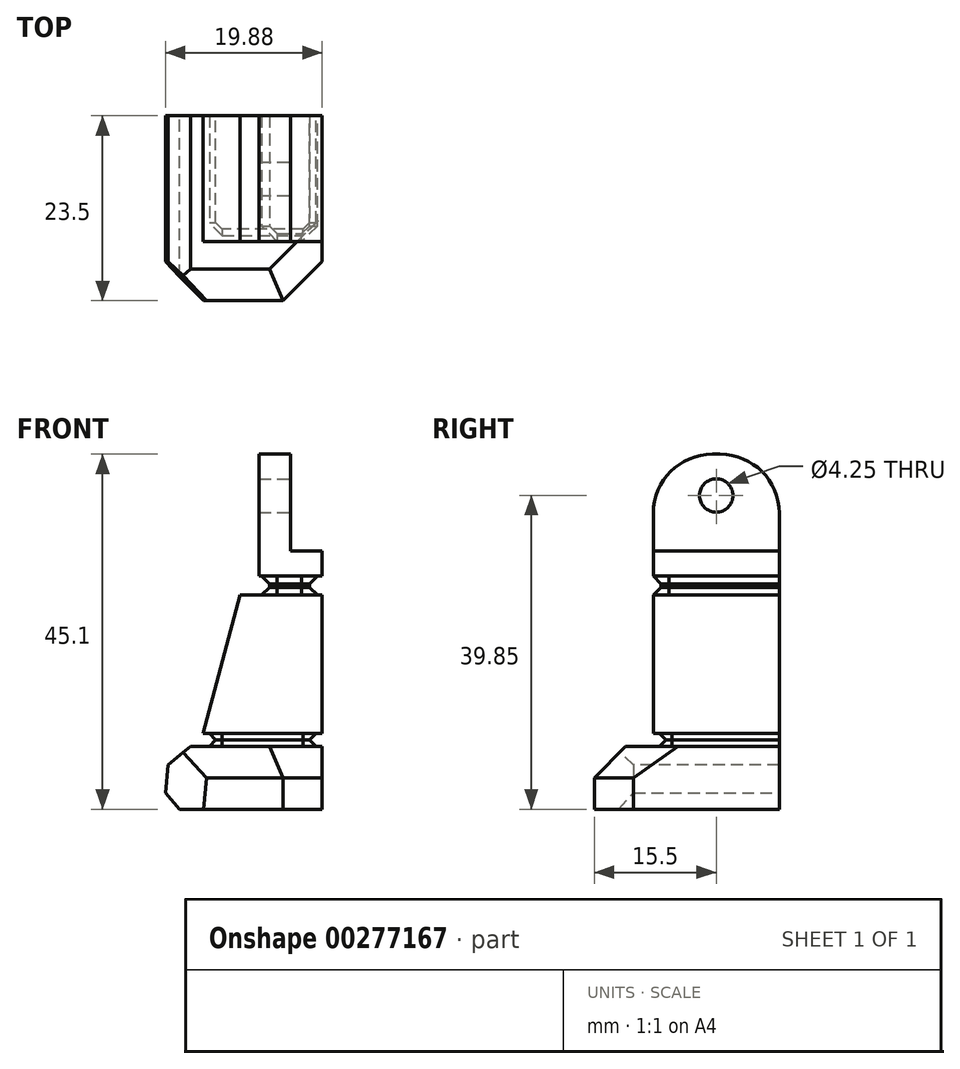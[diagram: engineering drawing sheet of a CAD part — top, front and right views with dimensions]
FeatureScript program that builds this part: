
annotation { "Feature Type Name" : "Feature", "Feature Type Description" : "" }
export const myFeature = defineFeature(function(context is Context, id is Id, definition is map)
    precondition{}
    {
        {
            var Q0;
            Q0=qCreatedBy(makeId("Front.planeOp"),FACE);
            var sketch = newSketch(context, id + "F0", { "sketchPlane" : qUnion([Q0])});
            skLineSegment(sketch, "E0.bottom", {"start": v(2, -5.25) * mm, "end": v(-2, -5.25) * mm});
            skLineSegment(sketch, "E0.top", {"start": v(2, 5.25) * mm, "end": v(-2, 5.25) * mm});
            skLineSegment(sketch, "E0.left", {"start": v(2, -5.25) * mm, "end": v(2, 5.25) * mm});
            skLineSegment(sketch, "E0.right", {"start": v(-2, -5.25) * mm, "end": v(-2, 5.25) * mm});
            skPoint(sketch, "E0.middle", {"position": v(0, 0) * mm});
            skSolve(sketch);
        }
        {
            var Q0;
            Q0=qSketchRegion(id+"F0",true);
            extrude(context, id + "F1", {"entities" : qUnion([Q0]), "endBound" : BoundingType.SYMMETRIC, "depth" : 16 * mm});
        }
        {
            var Q0;
            Q0=makeQuery(id+"F1.opExtrude","SWEPT_FACE",FACE,{"disambiguationData":[OSD([sQuery(id+"F0.wireOp",EDGE,"E0.left")])]});
            var sketch = newSketch(context, id + "F2", { "sketchPlane" : qUnion([Q0])});
            skCircle(sketch, "E1", {"center": v(0, 0) * mm, "radius": 2.13 * mm});
            skSolve(sketch);
        }
        {
            var Q0;
            Q0=qSketchRegion(id+"F2",true);
            extrude(context, id + "F3", {"entities" : qUnion([Q0]), "operationType" : NewBodyOperationType.REMOVE, "oppositeDirection" : true, "depth" : 4 * mm});
        }
        {
            var Q0;
            Q0=qCreatedBy(makeId("Front.planeOp"),FACE);
            var sketch = newSketch(context, id + "F4", { "sketchPlane" : qUnion([Q0])});
            skLineSegment(sketch, "E2", {"start": v(2, -5.25) * mm, "end": v(-2, -5.25) * mm});
            skLineSegment(sketch, "E3", {"start": v(-2, -5.25) * mm, "end": v(-2, -10.25) * mm});
            skLineSegment(sketch, "E4", {"start": v(-2, -10.25) * mm, "end": v(6, -10.25) * mm});
            skLineSegment(sketch, "E5", {"start": v(6, -10.25) * mm, "end": v(6, -7.05) * mm});
            skLineSegment(sketch, "E6", {"start": v(2, -5.25) * mm, "end": v(2, -7.05) * mm});
            skLineSegment(sketch, "E7", {"start": v(2, -7.05) * mm, "end": v(6, -7.05) * mm});
            skPoint(sketch, "E8.orphan", {"position": v(6, -5.25) * mm});
            skSolve(sketch);
        }
        {
            var Q0;
            Q0=qSketchRegion(id+"F4",true);
            extrude(context, id + "F5", {"entities" : qUnion([Q0]), "operationType" : NewBodyOperationType.ADD, "endBound" : BoundingType.SYMMETRIC, "depth" : 16 * mm});
        }
        {
            var Q0;
            Q0=qCreatedBy(makeId("Front.planeOp"),FACE);
            var sketch = newSketch(context, id + "F6", { "sketchPlane" : qUnion([Q0])});
            skLineSegment(sketch, "E9", {"start": v(-4.4, -12.65) * mm, "end": v(-9.12, -30.25) * mm});
            skLineSegment(sketch, "E10", {"start": v(-9.12, -30.25) * mm, "end": v(6, -30.25) * mm});
            skLineSegment(sketch, "E11", {"start": v(6, -30.25) * mm, "end": v(6, -12.65) * mm});
            skLineSegment(sketch, "E12", {"start": v(4.4, -10.25) * mm, "end": v(-0.7, -10.25) * mm});
            skLineSegment(sketch, "E13", {"start": v(6, -12.65) * mm, "end": v(4.4, -12.65) * mm});
            skLineSegment(sketch, "E14", {"start": v(4.4, -10.25) * mm, "end": v(4.4, -12.65) * mm});
            skLineSegment(sketch, "E15", {"start": v(-0.7, -10.25) * mm, "end": v(-0.7, -12.65) * mm});
            skLineSegment(sketch, "E16.trimOffspring", {"start": v(-0.7, -12.65) * mm, "end": v(-4.4, -12.65) * mm});
            skSolve(sketch);
        }
        {
            var Q0;
            Q0=qSketchRegion(id+"F6",true);
            extrude(context, id + "F7", {"entities" : qUnion([Q0]), "operationType" : NewBodyOperationType.ADD, "endBound" : BoundingType.SYMMETRIC, "depth" : 16 * mm});
        }
        {
            var Q0;
            Q0=makeQuery(id+"F7.boolean.opBoolean","MERGE",FACE,{"derivedFrom":[makeQuery(id+"F5.boolean.opBoolean","MERGE",FACE,{"derivedFrom":[makeQuery(id+"F1.opExtrude","CAP_FACE",FACE,{"disambiguationData":[OSD([sQuery(id+"F0.wireOp",EDGE,"E0.bottom"),sQuery(id+"F0.wireOp",EDGE,"E0.top"),sQuery(id+"F0.wireOp",EDGE,"E0.left"),sQuery(id+"F0.wireOp",EDGE,"E0.right")])],"isStart":false}),makeQuery(id+"F5.opExtrude","CAP_FACE",FACE,{"disambiguationData":[OSD([sQuery(id+"F4.wireOp",EDGE,"E2"),sQuery(id+"F4.wireOp",EDGE,"E3"),sQuery(id+"F4.wireOp",EDGE,"E4"),sQuery(id+"F4.wireOp",EDGE,"E5"),sQuery(id+"F4.wireOp",EDGE,"E6"),sQuery(id+"F4.wireOp",EDGE,"E7")])],"isStart":false})]}),makeQuery(id+"F7.opExtrude","CAP_FACE",FACE,{"disambiguationData":[OSD([sQuery(id+"F6.wireOp",EDGE,"E9"),sQuery(id+"F6.wireOp",EDGE,"E10"),sQuery(id+"F6.wireOp",EDGE,"E11"),sQuery(id+"F6.wireOp",EDGE,"E12"),sQuery(id+"F6.wireOp",EDGE,"E13"),sQuery(id+"F6.wireOp",EDGE,"E14"),sQuery(id+"F6.wireOp",EDGE,"E15"),sQuery(id+"F6.wireOp",EDGE,"E16.trimOffspring")])],"isStart":false})]});
            var sketch = newSketch(context, id + "F8", { "sketchPlane" : qUnion([Q0])});
            skLineSegment(sketch, "E17.bottom", {"start": v(-0.7, -10.25) * mm, "end": v(4.4, -10.25) * mm});
            skLineSegment(sketch, "E17.top", {"start": v(-0.7, -12.65) * mm, "end": v(4.4, -12.65) * mm});
            skLineSegment(sketch, "E17.left", {"start": v(-0.7, -10.25) * mm, "end": v(-0.7, -12.65) * mm});
            skLineSegment(sketch, "E17.right", {"start": v(4.4, -10.25) * mm, "end": v(4.4, -12.65) * mm});
            skSolve(sketch);
        }
        {
            var Q0;
            Q0=qSketchRegion(id+"F8",true);
            extrude(context, id + "F9", {"entities" : qUnion([Q0]), "operationType" : NewBodyOperationType.REMOVE, "oppositeDirection" : true, "depth" : 1 * mm});
        }
        {
            var Q0;
            Q0=makeQuery(id+"FqPLebVqW3BbuIx_1.1.F9.boolean.opBoolean","COPY",FACE,{"derivedFrom":makeQuery(id+"FqPLebVqW3BbuIx_1.1.F9.opExtrude","CAP_FACE",FACE,{"disambiguationData":[OSD([sQuery(id+"F8.wireOp",EDGE,"E17.bottom"),sQuery(id+"F8.wireOp",EDGE,"E17.top"),sQuery(id+"F8.wireOp",EDGE,"E17.left"),sQuery(id+"F8.wireOp",EDGE,"E17.right")])],"isStart":false})});
            var Q1;
            Q1=makeQuery(id+"F9.boolean.opBoolean","COPY",FACE,{"derivedFrom":makeQuery(id+"F9.opExtrude","CAP_FACE",FACE,{"disambiguationData":[OSD([sQuery(id+"F8.wireOp",EDGE,"E17.bottom"),sQuery(id+"F8.wireOp",EDGE,"E17.top"),sQuery(id+"F8.wireOp",EDGE,"E17.left"),sQuery(id+"F8.wireOp",EDGE,"E17.right")])],"isStart":false})});
            chamfer(context, id + "F10", {"entities" : qUnion([Q0, Q1]), "width" : 1 * mm, "tangentPropagation" : true});
        }
        {
            var Q0;
            Q0=qCreatedBy(makeId("Front.planeOp"),FACE);
            var sketch = newSketch(context, id + "F11", { "sketchPlane" : qUnion([Q0])});
            skLineSegment(sketch, "E18", {"start": v(4.4, -30.25) * mm, "end": v(4.4, -31.85) * mm});
            skLineSegment(sketch, "E19", {"start": v(4.4, -31.85) * mm, "end": v(6, -31.85) * mm});
            skLineSegment(sketch, "E20", {"start": v(6, -31.85) * mm, "end": v(6, -39.85) * mm});
            skLineSegment(sketch, "E21", {"start": v(6, -39.85) * mm, "end": v(-12.13, -39.85) * mm});
            skLineSegment(sketch, "E22", {"start": v(-12.13, -39.85) * mm, "end": v(-15.48, -35.85) * mm});
            skLineSegment(sketch, "E23", {"start": v(-15.48, -35.85) * mm, "end": v(-10.72, -31.85) * mm});
            skLineSegment(sketch, "E24", {"start": v(-10.72, -31.85) * mm, "end": v(-7.52, -31.85) * mm});
            skLineSegment(sketch, "E25", {"start": v(-7.52, -31.85) * mm, "end": v(-7.52, -30.25) * mm});
            skLineSegment(sketch, "E26", {"start": v(-7.52, -30.25) * mm, "end": v(4.4, -30.25) * mm});
            skSolve(sketch);
        }
        {
            var Q0;
            Q0=qSketchRegion(id+"F11",true);
            extrude(context, id + "F12", {"entities" : qUnion([Q0]), "operationType" : NewBodyOperationType.ADD, "endBound" : BoundingType.SYMMETRIC, "depth" : 16 * mm});
        }
        {
            var Q0;
            {var subQ0=sQuery(id+"F6.wireOp",EDGE,"E13");var subQ1=sQuery(id+"F6.wireOp",EDGE,"E16.trimOffspring");var subQ2=sQuery(id+"F6.wireOp",EDGE,"E11");var subQ3=sQuery(id+"F6.wireOp",EDGE,"E10");var subQ4=sQuery(id+"F6.wireOp",EDGE,"E9");Q0=makeQuery(id+"F12.boolean.opBoolean","MERGE",FACE,{"derivedFrom":[makeQuery(id+"F9.boolean.opBoolean","SPLIT",FACE,{"disambiguationData":[TD([makeQuery(id+"F7.opExtrude","SWEPT_FACE",FACE,{"disambiguationData":[OSD([subQ4])]})])],"derivedFrom":makeQuery(id+"F7.boolean.opBoolean","MERGE",FACE,{"derivedFrom":[makeQuery(id+"F5.boolean.opBoolean","MERGE",FACE,{"derivedFrom":[makeQuery(id+"F1.opExtrude","CAP_FACE",FACE,{"disambiguationData":[OSD([sQuery(id+"F0.wireOp",EDGE,"E0.bottom"),sQuery(id+"F0.wireOp",EDGE,"E0.top"),sQuery(id+"F0.wireOp",EDGE,"E0.left"),sQuery(id+"F0.wireOp",EDGE,"E0.right")])],"isStart":false}),makeQuery(id+"F5.opExtrude","CAP_FACE",FACE,{"disambiguationData":[OSD([sQuery(id+"F4.wireOp",EDGE,"E2"),sQuery(id+"F4.wireOp",EDGE,"E3"),sQuery(id+"F4.wireOp",EDGE,"E4"),sQuery(id+"F4.wireOp",EDGE,"E5"),sQuery(id+"F4.wireOp",EDGE,"E6"),sQuery(id+"F4.wireOp",EDGE,"E7")])],"isStart":false})]}),makeQuery(id+"F7.opExtrude","CAP_FACE",FACE,{"disambiguationData":[OSD([subQ4,subQ3,subQ2,sQuery(id+"F6.wireOp",EDGE,"E12"),subQ0,sQuery(id+"F6.wireOp",EDGE,"E14"),sQuery(id+"F6.wireOp",EDGE,"E15"),subQ1])],"isStart":false})]})}),makeQuery(id+"F12.opExtrude","CAP_FACE",FACE,{"disambiguationData":[OSD([sQuery(id+"F11.wireOp",EDGE,"E18"),sQuery(id+"F11.wireOp",EDGE,"E19"),sQuery(id+"F11.wireOp",EDGE,"E20"),sQuery(id+"F11.wireOp",EDGE,"E21"),sQuery(id+"F11.wireOp",EDGE,"E22"),sQuery(id+"F11.wireOp",EDGE,"E23"),sQuery(id+"F11.wireOp",EDGE,"E24"),sQuery(id+"F11.wireOp",EDGE,"E25"),sQuery(id+"F11.wireOp",EDGE,"E26")])],"isStart":false})]});}
            var sketch = newSketch(context, id + "F13", { "sketchPlane" : qUnion([Q0])});
            skLineSegment(sketch, "E27.bottom", {"start": v(-7.52, -30.25) * mm, "end": v(4.4, -30.25) * mm});
            skLineSegment(sketch, "E27.top", {"start": v(-7.52, -31.85) * mm, "end": v(4.4, -31.85) * mm});
            skLineSegment(sketch, "E27.left", {"start": v(-7.52, -30.25) * mm, "end": v(-7.52, -31.85) * mm});
            skLineSegment(sketch, "E27.right", {"start": v(4.4, -30.25) * mm, "end": v(4.4, -31.85) * mm});
            skSolve(sketch);
        }
        {
            var Q0;
            Q0=qSketchRegion(id+"F13",true);
            extrude(context, id + "F14", {"entities" : qUnion([Q0]), "operationType" : NewBodyOperationType.REMOVE, "oppositeDirection" : true, "depth" : 1.6 * mm});
        }
        {
            var Q0;
            {var subQ0=sQuery(id+"F11.wireOp",EDGE,"E21");var subQ1=sQuery(id+"F11.wireOp",EDGE,"E20");var subQ2=sQuery(id+"F11.wireOp",EDGE,"E22");var subQ3=sQuery(id+"F11.wireOp",EDGE,"E19");var subQ4=sQuery(id+"F11.wireOp",EDGE,"E24");var subQ5=sQuery(id+"F11.wireOp",EDGE,"E23");var subQ6=sQuery(id+"F6.wireOp",EDGE,"E13");var subQ7=sQuery(id+"F6.wireOp",EDGE,"E16.trimOffspring");var subQ8=sQuery(id+"F6.wireOp",EDGE,"E11");var subQ9=sQuery(id+"F6.wireOp",EDGE,"E10");var subQ10=sQuery(id+"F6.wireOp",EDGE,"E9");Q0=makeQuery(id+"F14.boolean.opBoolean","SPLIT",FACE,{"disambiguationData":[TD([makeQuery(id+"F12.opExtrude","SWEPT_FACE",FACE,{"disambiguationData":[OSD([subQ3])]})])],"derivedFrom":makeQuery(id+"F12.boolean.opBoolean","MERGE",FACE,{"derivedFrom":[makeQuery(id+"F9.boolean.opBoolean","SPLIT",FACE,{"disambiguationData":[TD([makeQuery(id+"F7.opExtrude","SWEPT_FACE",FACE,{"disambiguationData":[OSD([subQ10])]})])],"derivedFrom":makeQuery(id+"F7.boolean.opBoolean","MERGE",FACE,{"derivedFrom":[makeQuery(id+"F5.boolean.opBoolean","MERGE",FACE,{"derivedFrom":[makeQuery(id+"F1.opExtrude","CAP_FACE",FACE,{"disambiguationData":[OSD([sQuery(id+"F0.wireOp",EDGE,"E0.bottom"),sQuery(id+"F0.wireOp",EDGE,"E0.top"),sQuery(id+"F0.wireOp",EDGE,"E0.left"),sQuery(id+"F0.wireOp",EDGE,"E0.right")])],"isStart":false}),makeQuery(id+"F5.opExtrude","CAP_FACE",FACE,{"disambiguationData":[OSD([sQuery(id+"F4.wireOp",EDGE,"E2"),sQuery(id+"F4.wireOp",EDGE,"E3"),sQuery(id+"F4.wireOp",EDGE,"E4"),sQuery(id+"F4.wireOp",EDGE,"E5"),sQuery(id+"F4.wireOp",EDGE,"E6"),sQuery(id+"F4.wireOp",EDGE,"E7")])],"isStart":false})]}),makeQuery(id+"F7.opExtrude","CAP_FACE",FACE,{"disambiguationData":[OSD([subQ10,subQ9,subQ8,sQuery(id+"F6.wireOp",EDGE,"E12"),subQ6,sQuery(id+"F6.wireOp",EDGE,"E14"),sQuery(id+"F6.wireOp",EDGE,"E15"),subQ7])],"isStart":false})]})}),makeQuery(id+"F12.opExtrude","CAP_FACE",FACE,{"disambiguationData":[OSD([sQuery(id+"F11.wireOp",EDGE,"E18"),subQ3,subQ1,subQ0,subQ2,subQ5,subQ4,sQuery(id+"F11.wireOp",EDGE,"E25"),sQuery(id+"F11.wireOp",EDGE,"E26")])],"isStart":false})]})});}
            var sketch = newSketch(context, id + "F15", { "sketchPlane" : qUnion([Q0])});
            skLineSegment(sketch, "E28", {"start": v(-15.48, -35.85) * mm, "end": v(-12.13, -39.85) * mm});
            skLineSegment(sketch, "E29", {"start": v(-12.13, -39.85) * mm, "end": v(6, -39.85) * mm});
            skLineSegment(sketch, "E30", {"start": v(6, -39.85) * mm, "end": v(6, -31.85) * mm});
            skLineSegment(sketch, "E31", {"start": v(6, -31.85) * mm, "end": v(-10.72, -31.85) * mm});
            skLineSegment(sketch, "E32", {"start": v(-10.72, -31.85) * mm, "end": v(-15.48, -35.85) * mm});
            skSolve(sketch);
        }
        {
            var Q0;
            Q0=qSketchRegion(id+"F15",true);
            extrude(context, id + "F16", {"entities" : qUnion([Q0]), "operationType" : NewBodyOperationType.ADD, "depth" : 7.5 * mm});
        }
        {
            var Q0;
            Q0=makeQuery(id+"F16.opExtrude","CAP_EDGE",EDGE,{"disambiguationData":[OSD([sQuery(id+"F15.wireOp",EDGE,"E30")])],"isStart":false});
            chamfer(context, id + "F17", {"entities" : qUnion([Q0]), "width" : 5 * mm, "tangentPropagation" : true});
        }
        {
            var Q0;
            Q0=makeQuery(id+"F16.opExtrude","CAP_EDGE",EDGE,{"disambiguationData":[OSD([sQuery(id+"F15.wireOp",EDGE,"E31")])],"isStart":false});
            var Q1;
            {var subQ0=sQuery(id+"F13.wireOp",EDGE,"E27.top");Q1=makeQuery(id+"F17.opChamfer","BLEND_EDGE",EDGE,{"blendedFrom":[makeQuery(id+"F16.opExtrude","CAP_EDGE",EDGE,{"disambiguationData":[OSD([sQuery(id+"F15.wireOp",EDGE,"E30")])],"isStart":false}),makeQuery(id+"F16.boolean.opBoolean","MERGE",FACE,{"derivedFrom":[makeQuery(id+"FDENq49OKnNjuyT_1.1.F14.boolean.opBoolean","MERGE",FACE,{"derivedFrom":[makeQuery(id+"F14.boolean.opBoolean","MERGE",FACE,{"derivedFrom":[makeQuery(id+"F12.opExtrude","SWEPT_FACE",FACE,{"disambiguationData":[OSD([sQuery(id+"F11.wireOp",EDGE,"E19")])]}),makeQuery(id+"F12.opExtrude","SWEPT_FACE",FACE,{"disambiguationData":[OSD([sQuery(id+"F11.wireOp",EDGE,"E24")])]}),makeQuery(id+"F14.opExtrude","SWEPT_FACE",FACE,{"disambiguationData":[OSD([subQ0])]})]}),makeQuery(id+"FDENq49OKnNjuyT_1.1.F14.opExtrude","SWEPT_FACE",FACE,{"disambiguationData":[OSD([subQ0])]})]}),makeQuery(id+"F16.opExtrude","SWEPT_FACE",FACE,{"disambiguationData":[OSD([sQuery(id+"F15.wireOp",EDGE,"E31")])]})]})],"blendedInto":[makeQuery(id+"F16.boolean.opBoolean","MERGE",FACE,{"derivedFrom":[makeQuery(id+"FDENq49OKnNjuyT_1.1.F14.boolean.opBoolean","MERGE",FACE,{"derivedFrom":[makeQuery(id+"F14.boolean.opBoolean","MERGE",FACE,{"derivedFrom":[makeQuery(id+"F12.opExtrude","SWEPT_FACE",FACE,{"disambiguationData":[OSD([sQuery(id+"F11.wireOp",EDGE,"E19")])]}),makeQuery(id+"F12.opExtrude","SWEPT_FACE",FACE,{"disambiguationData":[OSD([sQuery(id+"F11.wireOp",EDGE,"E24")])]}),makeQuery(id+"F14.opExtrude","SWEPT_FACE",FACE,{"disambiguationData":[OSD([subQ0])]})]}),makeQuery(id+"FDENq49OKnNjuyT_1.1.F14.opExtrude","SWEPT_FACE",FACE,{"disambiguationData":[OSD([subQ0])]})]}),makeQuery(id+"F16.opExtrude","SWEPT_FACE",FACE,{"disambiguationData":[OSD([sQuery(id+"F15.wireOp",EDGE,"E31")])]})]})]});}
            chamfer(context, id + "F18", {"entities" : qUnion([Q0, Q1]), "width" : 4 * mm, "tangentPropagation" : true});
        }
        {
            var Q0;
            Q0=makeQuery(id+"F16.boolean.opBoolean","MERGE",EDGE,{"derivedFrom":[makeQuery(id+"F12.opExtrude","SWEPT_EDGE",EDGE,{"disambiguationData":[OSD([sQuery(id+"F11.wireOp",EDGE,"E22"),sQuery(id+"F11.wireOp",EDGE,"E23")])]}),makeQuery(id+"F16.opExtrude","SWEPT_EDGE",EDGE,{"disambiguationData":[OSD([sQuery(id+"F15.wireOp",EDGE,"hGkAko4b-c8oI-brO5-s9bs-4SnFjtLzBies"),sQuery(id+"F15.wireOp",EDGE,"E28")])]})]});
            chamfer(context, id + "F19", {"entities" : qUnion([Q0]), "width" : 2.5 * mm, "tangentPropagation" : true});
        }
        {
            var Q0;
            {var subQ0=sQuery(id+"F15.wireOp",EDGE,"E28");var subQ1=sQuery(id+"F15.wireOp",EDGE,"hGkAko4b-c8oI-brO5-s9bs-4SnFjtLzBies");Q0=makeQuery(id+"F19.opChamfer","BLEND_EDGE",EDGE,{"blendedFrom":[makeQuery(id+"F16.boolean.opBoolean","MERGE",EDGE,{"derivedFrom":[makeQuery(id+"F12.opExtrude","SWEPT_EDGE",EDGE,{"disambiguationData":[OSD([sQuery(id+"F11.wireOp",EDGE,"E22"),sQuery(id+"F11.wireOp",EDGE,"E23")])]}),makeQuery(id+"F16.opExtrude","SWEPT_EDGE",EDGE,{"disambiguationData":[OSD([subQ1,subQ0])]})]}),makeQuery(id+"F16.opExtrude","CAP_FACE",FACE,{"disambiguationData":[OSD([subQ1,subQ0,sQuery(id+"F15.wireOp",EDGE,"E29"),sQuery(id+"F15.wireOp",EDGE,"E30"),sQuery(id+"F15.wireOp",EDGE,"E31")])],"isStart":false})],"blendedInto":[makeQuery(id+"F16.opExtrude","CAP_FACE",FACE,{"disambiguationData":[OSD([subQ1,subQ0,sQuery(id+"F15.wireOp",EDGE,"E29"),sQuery(id+"F15.wireOp",EDGE,"E30"),sQuery(id+"F15.wireOp",EDGE,"E31")])],"isStart":false})]});}
            chamfer(context, id + "F20", {"entities" : qUnion([Q0]), "width" : 5 * mm, "tangentPropagation" : true});
        }
        {
            var Q0;
            Q0=makeQuery(id+"F14.boolean.opBoolean","COPY",FACE,{"derivedFrom":makeQuery(id+"F14.opExtrude","CAP_FACE",FACE,{"disambiguationData":[OSD([sQuery(id+"F13.wireOp",EDGE,"E27.bottom"),sQuery(id+"F13.wireOp",EDGE,"E27.top"),sQuery(id+"F13.wireOp",EDGE,"E27.left"),sQuery(id+"F13.wireOp",EDGE,"E27.right")])],"isStart":false})});
            var Q1;
            Q1=makeQuery(id+"FDENq49OKnNjuyT_1.1.F14.boolean.opBoolean","COPY",FACE,{"derivedFrom":makeQuery(id+"FDENq49OKnNjuyT_1.1.F14.opExtrude","CAP_FACE",FACE,{"disambiguationData":[OSD([sQuery(id+"F13.wireOp",EDGE,"E27.bottom"),sQuery(id+"F13.wireOp",EDGE,"E27.top"),sQuery(id+"F13.wireOp",EDGE,"E27.left"),sQuery(id+"F13.wireOp",EDGE,"E27.right")])],"isStart":false})});
            chamfer(context, id + "F21", {"entities" : qUnion([Q0, Q1]), "width" : .8 * mm, "tangentPropagation" : true});
        }
        {
            var Q0;
            Q0=makeQuery(id+"F1.opExtrude","CAP_EDGE",EDGE,{"disambiguationData":[OSD([sQuery(id+"F0.wireOp",EDGE,"E0.top")])],"isStart":true});
            var Q1;
            Q1=makeQuery(id+"F1.opExtrude","CAP_EDGE",EDGE,{"disambiguationData":[OSD([sQuery(id+"F0.wireOp",EDGE,"E0.top")])],"isStart":false});
            fillet(context, id + "F22", {"entities" : qUnion([Q0, Q1]), "radius" : 7.5 * mm, "tangentPropagation" : true, "allowEdgeOverflow" : false});
        }
    });
